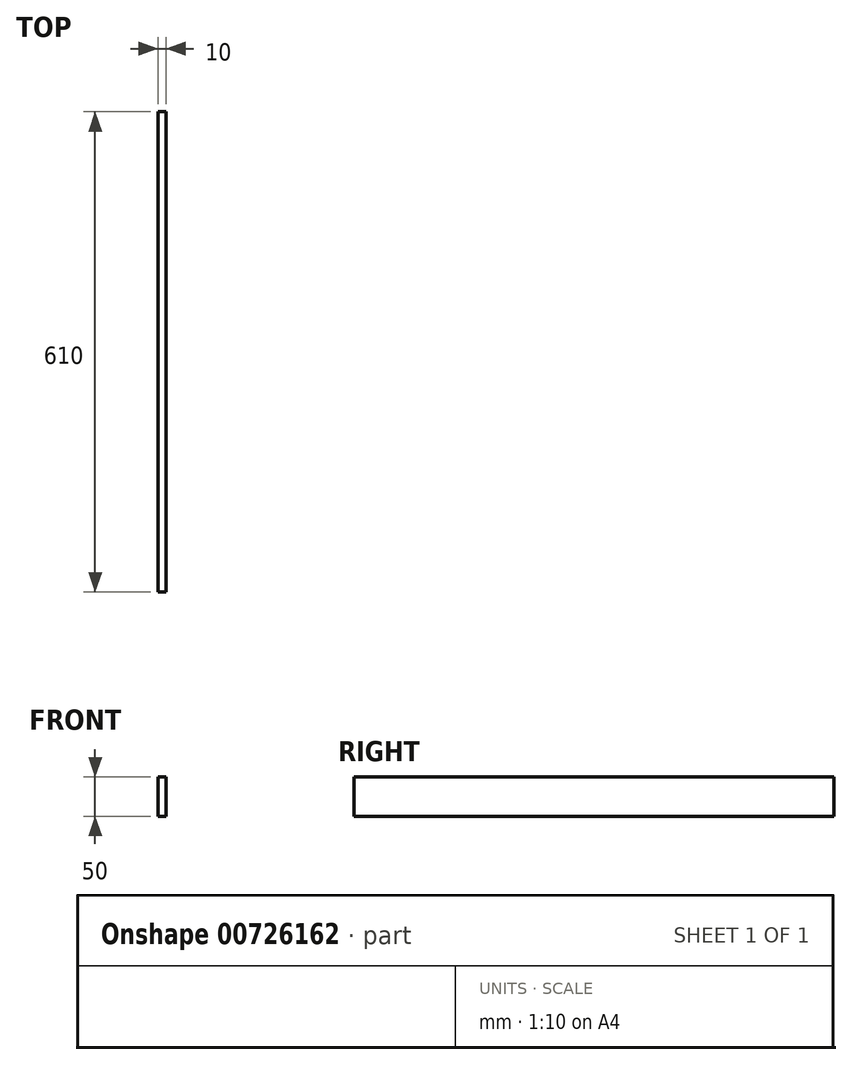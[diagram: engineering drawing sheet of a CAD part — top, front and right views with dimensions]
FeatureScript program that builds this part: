
annotation { "Feature Type Name" : "Feature", "Feature Type Description" : "" }
export const myFeature = defineFeature(function(context is Context, id is Id, definition is map)
    precondition{}
    {
        {
            var Q0;
            Q0=qCreatedBy(makeId("Right.planeOp"),FACE);
            var sketch = newSketch(context, id + "F0", { "sketchPlane" : qUnion([Q0])});
            skLineSegment(sketch, "E0.bottom", {"start": v(-305, 25) * mm, "end": v(305, 25) * mm});
            skLineSegment(sketch, "E0.top", {"start": v(-305, -25) * mm, "end": v(305, -25) * mm});
            skLineSegment(sketch, "E0.left", {"start": v(-305, 25) * mm, "end": v(-305, -25) * mm});
            skLineSegment(sketch, "E0.right", {"start": v(305, 25) * mm, "end": v(305, -25) * mm});
            skLineSegment(sketch, "E1", {"start": v(0, -25) * mm, "end": v(0, 25) * mm, "construction": true});
            skSolve(sketch);
        }
        {
            var Q0;
            Q0 = qSketchRegion(id + "F0", true);
            extrude(context, id + "F1", {"entities" : qUnion([Q0]), "depth" : 10 * mm, "offsetDistance" : 25 * mm});
        }
    });
